# Revit family: Accessory-Valve_Trim-KALLISTA-Aileron-P39847-1
name_source: partatom
category: Specialty Equipment
units: mm (PartAtom-declared; Revit-internal decimal feet)

## family parameters
Cut with Voids When Loaded = No
Host = Face
Maintain Annotation Orientation = No
OmniClass Number = 23.31.25.00
OmniClass Title = Toilet and Bath Specialties
Part Type = Normal
Room Calculation Point = No
Round Connector Dimension = Use Diameter
Shared = No

## types (6) — shared parameters
ADA Compliant = No
Assembly Code = C1030200
Date Modified = 08/19/2025
Default Elevation = 42"
Description = 2-Outlet Stacked Thermostatic Trim Lever Handle
Handle Clearance = 1 7/8"
Height = 7 7/8"
Manufacturer = Kallista Co.
Master Format 2014 = 10 28 00
Master Format 2014 Name = Toilet, Bath, and Laundry Accessories
Material = Premium Metal Contruction
Product Name = Aileron
URL = https://www.kallista.com
WaterSense Certified = No
Width = 4 3/4"

## per-type parameters (varying)
| type | Finish | Model | Type |
| 2MB-Brushed Brass | Kallista-Metal-2MB-Brushed_Brass | P39847-LV-2MB | 1 |
| BGP-Brushed Graphite | Kallista-Metal-BGP-Brushed_Graphite | P39847-LV-BGP | 2 |
| BL-Matte Black | Kallista-Metal-BL-Matte_Black | P39847-LV-BL | 3 |
| BLH-Blush Brass | Kallista-Metal-BLH-Blush_Brass | P39847-LV-BLH | 4 |
| BN-Brushed Nickel | Kallista-Metal-BN-Brushed_Nickel | P39847-LV-BN | 5 |
| CP-Chrome | Kallista-Metal-CP-Chrome | P39847-LV-CP | 6 |

## geometry (parser evidence)
native form markers: Sweep x6
no freeform markers — native parametric forms only
